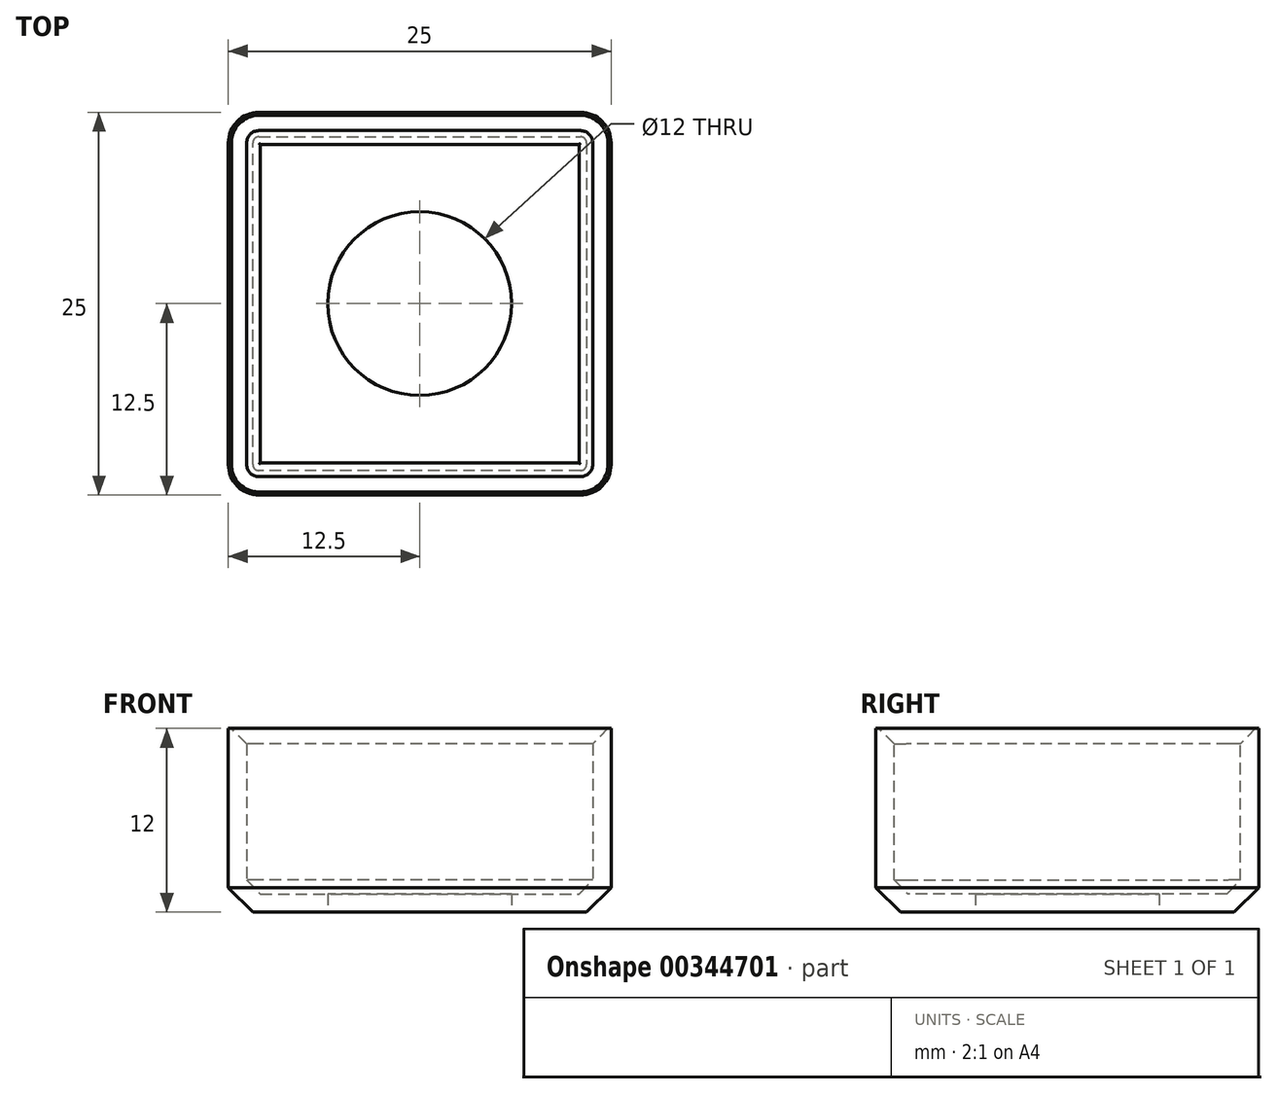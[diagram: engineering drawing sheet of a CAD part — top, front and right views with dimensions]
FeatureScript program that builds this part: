
annotation { "Feature Type Name" : "Feature", "Feature Type Description" : "" }
export const myFeature = defineFeature(function(context is Context, id is Id, definition is map)
    precondition{}
    {
        {
            var Q0;
            Q0=qCreatedBy(makeId("Top.planeOp"),FACE);
            var sketch = newSketch(context, id + "F0", { "sketchPlane" : qUnion([Q0])});
            skLineSegment(sketch, "E0.bottom", {"start": v(-12.5, 12.5) * mm, "end": v(12.5, 12.5) * mm});
            skLineSegment(sketch, "E0.top", {"start": v(-12.5, -12.5) * mm, "end": v(12.5, -12.5) * mm});
            skLineSegment(sketch, "E0.left", {"start": v(-12.5, 12.5) * mm, "end": v(-12.5, -12.5) * mm});
            skLineSegment(sketch, "E0.right", {"start": v(12.5, 12.5) * mm, "end": v(12.5, -12.5) * mm});
            skSolve(sketch);
        }
        {
            var Q0;
            Q0 = qSketchRegion(id + "F0", true);
            extrude(context, id + "F1", {"entities" : qUnion([Q0]), "depth" : 12 * mm});
        }
        {
            var Q0;
            Q0=makeQuery(id+"F1.opExtrude","SWEPT_EDGE",EDGE,{"disambiguationData":[OSD([sQuery(id+"F0.wireOp",EDGE,"E0.top"),sQuery(id+"F0.wireOp",EDGE,"E0.left")])]});
            var Q1;
            Q1=makeQuery(id+"F1.opExtrude","SWEPT_EDGE",EDGE,{"disambiguationData":[OSD([sQuery(id+"F0.wireOp",EDGE,"E0.top"),sQuery(id+"F0.wireOp",EDGE,"E0.right")])]});
            var Q2;
            Q2=makeQuery(id+"F1.opExtrude","SWEPT_EDGE",EDGE,{"disambiguationData":[OSD([sQuery(id+"F0.wireOp",EDGE,"E0.bottom"),sQuery(id+"F0.wireOp",EDGE,"E0.right")])]});
            var Q3;
            Q3=makeQuery(id+"F1.opExtrude","SWEPT_EDGE",EDGE,{"disambiguationData":[OSD([sQuery(id+"F0.wireOp",EDGE,"E0.bottom"),sQuery(id+"F0.wireOp",EDGE,"E0.left")])]});
            fillet(context, id + "F2", {"entities" : qUnion([Q0, Q1, Q2, Q3]), "radius" : 2 * mm, "tangentPropagation" : true, "allowEdgeOverflow" : false});
        }
        {
            var Q0;
            Q0=makeQuery(id+"F1.opExtrude","CAP_FACE",FACE,{"disambiguationData":[OSD([sQuery(id+"F0.wireOp",EDGE,"E0.bottom"),sQuery(id+"F0.wireOp",EDGE,"E0.top"),sQuery(id+"F0.wireOp",EDGE,"E0.left"),sQuery(id+"F0.wireOp",EDGE,"E0.right")])],"isStart":true});
            chamfer(context, id + "F3", {"entities" : qUnion([Q0]), "width" : 1.6 * mm, "tangentPropagation" : true});
        }
        {
            var Q0;
            Q0=makeQuery(id+"F1.opExtrude","CAP_FACE",FACE,{"disambiguationData":[OSD([sQuery(id+"F0.wireOp",EDGE,"E0.bottom"),sQuery(id+"F0.wireOp",EDGE,"E0.top"),sQuery(id+"F0.wireOp",EDGE,"E0.left"),sQuery(id+"F0.wireOp",EDGE,"E0.right")])],"isStart":false});
            shell(context, id + "F4", {"entities" : qUnion([Q0]), "thickness" : 1.2 * mm});
        }
        {
            var Q0;
            {var subQ0=sQuery(id+"F0.wireOp",EDGE,"E0.bottom");Q0=makeQuery(id+"F4.opShell","OFFSET_EDGE",EDGE,{"disambiguationData":[OSD([subQ0]),TDD([makeQuery(id+"F1.opExtrude","CAP_EDGE",EDGE,{"disambiguationData":[OSD([subQ0])],"isStart":false})])]});}
            chamfer(context, id + "F5", {"entities" : qUnion([Q0]), "width" : 1 * mm, "tangentPropagation" : true});
        }
        {
            var Q0;
            Q0=qCreatedBy(makeId("Top.planeOp"),FACE);
            var sketch = newSketch(context, id + "F6", { "sketchPlane" : qUnion([Q0])});
            skCircle(sketch, "E1", {"center": v(0, 0) * mm, "radius": 6 * mm});
            skSolve(sketch);
        }
        {
            var Q0;
            Q0 = qSketchRegion(id + "F6", true);
            extrude(context, id + "F7", {"entities" : qUnion([Q0]), "operationType" : NewBodyOperationType.REMOVE, "depth" : 25 * mm});
        }
    });
